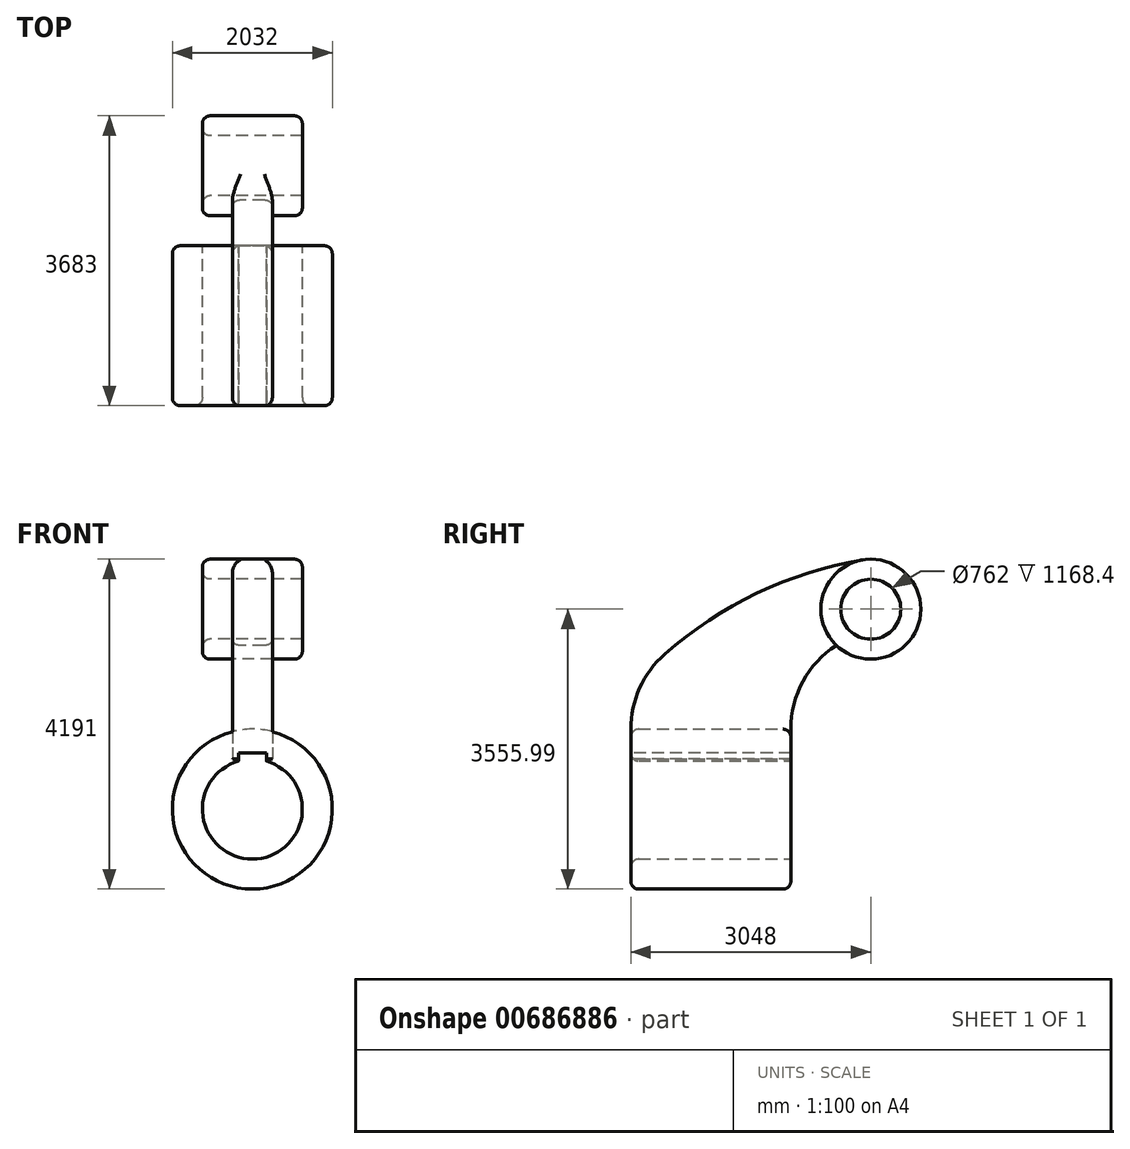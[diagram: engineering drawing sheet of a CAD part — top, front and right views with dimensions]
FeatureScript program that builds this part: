
annotation { "Feature Type Name" : "Feature", "Feature Type Description" : "" }
export const myFeature = defineFeature(function(context is Context, id is Id, definition is map)
    precondition{}
    {
        {
            var Q0;
            Q0=qCreatedBy(makeId("Right.planeOp"),FACE);
            var sketch = newSketch(context, id + "F0", { "sketchPlane" : qUnion([Q0])});
            skCircle(sketch, "E0", {"center": v(1016, 2693.13) * mm, "radius": 381 * mm});
            skCircle(sketch, "E1", {"center": v(1016, 2693.13) * mm, "radius": 635 * mm});
            skLineSegment(sketch, "E2", {"start": v(4389.62, 153.13) * mm, "end": v(-6696.81, 153.13) * mm, "construction": true});
            skLineSegment(sketch, "E3.bottom", {"start": v(-2032, 1169.13) * mm, "end": v(0, 1169.13) * mm});
            skLineSegment(sketch, "E3.top", {"start": v(-2032, 788.13) * mm, "end": v(0, 788.13) * mm});
            skLineSegment(sketch, "E3.left", {"start": v(-2032, 1169.13) * mm, "end": v(-2032, 788.13) * mm});
            skLineSegment(sketch, "E3.right", {"start": v(0, 1169.13) * mm, "end": v(0, 788.13) * mm});
            skLineSegment(sketch, "E4", {"start": v(1016, 2693.13) * mm, "end": v(1016, -726.15) * mm, "construction": true});
            skArc(sketch, "E5", {"start": v(577.58, 2233.76) * mm, "mid": v(153.7, 1774.74) * mm, "end": v(0, 1169.13) * mm});
            skArc(sketch, "E6", {"start": v(-1601.5, 2122.09) * mm, "mid": v(-1919.38, 1691.97) * mm, "end": v(-2032, 1169.13) * mm});
            skArc(sketch, "E7", {"start": v(910.21, 3319.25) * mm, "mid": v(-429.2, 2895.99) * mm, "end": v(-1601.5, 2122.09) * mm});
            skSolve(sketch);
        }
        {
            var Q0;
            Q0=makeQuery(id+"F0.imprint","IMPRINT",FACE,{"disambiguationData":[TD([[makeQuery(id+"F0.imprint","IMPRINT",EDGE,{"derivedFrom":sQuery(id+"F0.wireOp",EDGE,"E3.bottom")}),-1.0]])]});
            var Q1;
            Q1=sQuery(id+"F0.wireOp",EDGE,"E2");
            revolve(context, id + "F1", {"entities" : qUnion([Q0]), "axis" : qUnion([Q1]), "revolveType" : RevolveType.FULL});
        }
        {
            var Q0;
            Q0=makeQuery(id+"F0.imprint","IMPRINT",FACE,{"disambiguationData":[TD([[makeQuery(id+"F0.imprint","IMPRINT",EDGE,{"derivedFrom":sQuery(id+"F0.wireOp",EDGE,"E3.bottom")}),-1.0]])]});
            var Q1;
            Q1=makeQuery(id+"F0.imprint","IMPRINT",FACE,{"disambiguationData":[TD([[makeQuery(id+"F0.imprint","IMPRINT",EDGE,{"derivedFrom":sQuery(id+"F0.wireOp",EDGE,"E3.bottom")}),1.0]])]});
            extrude(context, id + "F2", {"entities" : qUnion([Q0, Q1]), "endBound" : BoundingType.SYMMETRIC, "depth" : 508 * mm, "offsetDistance" : 25.4 * mm});
        }
        {
            var Q0;
            Q0=makeQuery(id+"F0.imprint","IMPRINT",FACE,{"disambiguationData":[TD([[makeQuery(id+"F0.imprint","IMPRINT",EDGE,{"derivedFrom":sQuery(id+"F0.wireOp",EDGE,"E0")}),-1.0]])]});
            extrude(context, id + "F3", {"entities" : qUnion([Q0]), "operationType" : NewBodyOperationType.ADD, "endBound" : BoundingType.SYMMETRIC, "depth" : 1270 * mm, "offsetDistance" : 25.4 * mm});
        }
        {
            var Q0;
            Q0=makeQuery(id+"F2.opExtrude","CAP_EDGE",EDGE,{"disambiguationData":[OSD([sQuery(id+"F0.wireOp",EDGE,"E7")])],"isStart":false});
            var Q1;
            Q1=makeQuery(id+"F2.opExtrude","CAP_EDGE",EDGE,{"disambiguationData":[OSD([sQuery(id+"F0.wireOp",EDGE,"E7")])],"isStart":true});
            var Q2;
            Q2=makeQuery(id+"F2.opExtrude","CAP_EDGE",EDGE,{"disambiguationData":[OSD([sQuery(id+"F0.wireOp",EDGE,"E6")])],"isStart":true});
            var Q3;
            Q3=makeQuery(id+"F1.opRevolve","SWEPT_EDGE",EDGE,{"disambiguationData":[OSD([sQuery(id+"F0.wireOp",EDGE,"E3.bottom"),sQuery(id+"F0.wireOp",EDGE,"E3.left"),sQuery(id+"F0.wireOp",EDGE,"E6")])]});
            var Q4;
            Q4=makeQuery(id+"F3.opExtrude","CAP_EDGE",EDGE,{"disambiguationData":[OSD([sQuery(id+"F0.wireOp",EDGE,"E1")])],"isStart":false});
            var Q5;
            Q5=makeQuery(id+"F3.opExtrude","CAP_EDGE",EDGE,{"disambiguationData":[OSD([sQuery(id+"F0.wireOp",EDGE,"E1")])],"isStart":true});
            var Q6;
            Q6=makeQuery(id+"F3.opExtrude","CAP_EDGE",EDGE,{"disambiguationData":[OSD([sQuery(id+"F0.wireOp",EDGE,"E0")])],"isStart":true});
            var Q7;
            Q7=makeQuery(id+"F1.opRevolve","SWEPT_EDGE",EDGE,{"disambiguationData":[OSD([sQuery(id+"F0.wireOp",EDGE,"E3.bottom"),sQuery(id+"F0.wireOp",EDGE,"E3.right"),sQuery(id+"F0.wireOp",EDGE,"E5")])]});
            var Q8;
            Q8=makeQuery(id+"F1.opRevolve","SWEPT_EDGE",EDGE,{"disambiguationData":[OSD([sQuery(id+"F0.wireOp",EDGE,"E3.top"),sQuery(id+"F0.wireOp",EDGE,"E3.left")])]});
            var Q9;
            Q9=makeQuery(id+"F2.opExtrude","CAP_EDGE",EDGE,{"disambiguationData":[OSD([sQuery(id+"F0.wireOp",EDGE,"E5")])],"isStart":true});
            var Q10;
            Q10=makeQuery(id+"F2.opExtrude","CAP_EDGE",EDGE,{"disambiguationData":[OSD([sQuery(id+"F0.wireOp",EDGE,"E5")])],"isStart":false});
            var Q11;
            Q11=makeQuery(id+"F2.opExtrude","CAP_EDGE",EDGE,{"disambiguationData":[OSD([sQuery(id+"F0.wireOp",EDGE,"E1")])],"isStart":true});
            var Q12;
            Q12=makeQuery(id+"F2.opExtrude","CAP_EDGE",EDGE,{"disambiguationData":[OSD([sQuery(id+"F0.wireOp",EDGE,"E1")])],"isStart":false});
            fillet(context, id + "F4", {"entities" : qUnion([Q0, Q1, Q2, Q3, Q4, Q5, Q6, Q7, Q8, Q9, Q10, Q11, Q12]), "radius" : 101.6 * mm, "tangentPropagation" : true, "allowEdgeOverflow" : false});
        }
        {
            var Q0;
            Q0=makeQuery(id+"F1.opRevolve","SWEPT_FACE",FACE,{"disambiguationData":[OSD([sQuery(id+"F0.wireOp",EDGE,"E3.left")])]});
            var sketch = newSketch(context, id + "F5", { "sketchPlane" : qUnion([Q0])});
            skLineSegment(sketch, "E8.bottom", {"start": v(177.8, 867.94) * mm, "end": v(-177.8, 867.94) * mm});
            skLineSegment(sketch, "E8.top", {"start": v(177.8, 105.94) * mm, "end": v(-177.8, 105.94) * mm});
            skLineSegment(sketch, "E8.left", {"start": v(177.8, 867.94) * mm, "end": v(177.8, 105.94) * mm});
            skLineSegment(sketch, "E8.right", {"start": v(-177.8, 867.94) * mm, "end": v(-177.8, 105.94) * mm});
            skPoint(sketch, "E8.middle", {"position": v(0, 486.94) * mm});
            skSolve(sketch);
        }
        {
            var Q0;
            Q0=makeQuery(id+"F5.imprint","IMPRINT",FACE,{"disambiguationData":[TD([[makeQuery(id+"F5.imprint","IMPRINT",EDGE,{"derivedFrom":sQuery(id+"F5.wireOp",EDGE,"E8.bottom")}),1.0]])]});
            extrude(context, id + "F6", {"entities" : qUnion([Q0]), "operationType" : NewBodyOperationType.REMOVE, "oppositeDirection" : true, "depth" : 2032 * mm, "offsetDistance" : 25.4 * mm});
        }
    });
